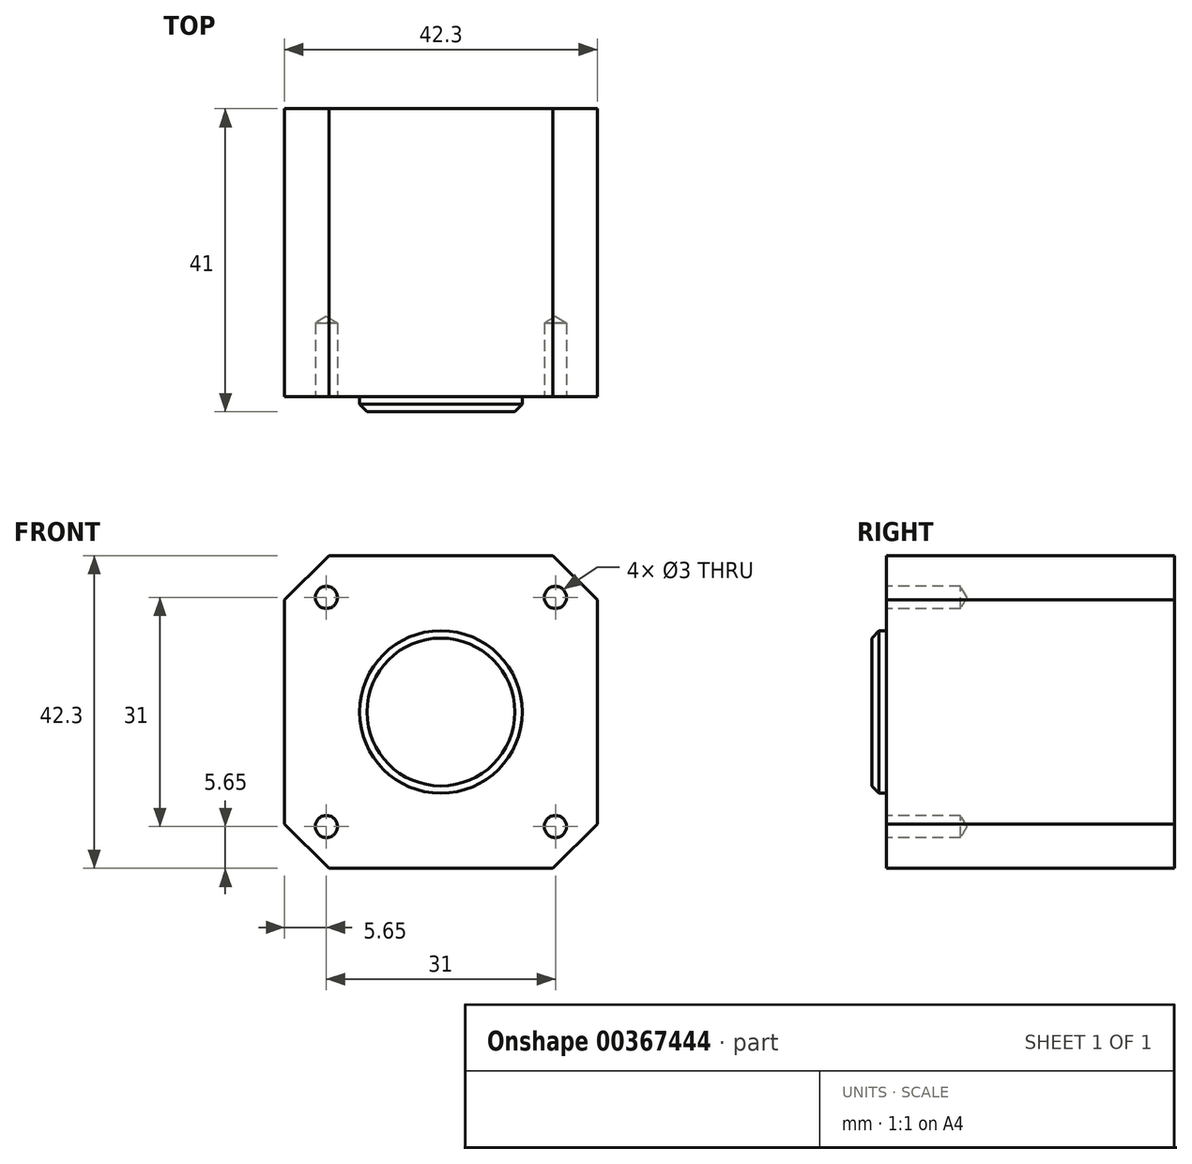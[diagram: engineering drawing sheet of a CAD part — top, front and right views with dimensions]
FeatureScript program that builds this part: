
annotation { "Feature Type Name" : "Feature", "Feature Type Description" : "" }
export const myFeature = defineFeature(function(context is Context, id is Id, definition is map)
    precondition{}
    {
        {
            var Q0;
            Q0=qCreatedBy(makeId("Front.planeOp"),FACE);
            var sketch = newSketch(context, id + "F0", { "sketchPlane" : qUnion([Q0])});
            skLineSegment(sketch, "E0.bottom", {"start": v(0, 0) * mm, "end": v(42.3, 0) * mm});
            skLineSegment(sketch, "E0.top", {"start": v(0, 42.3) * mm, "end": v(42.3, 42.3) * mm});
            skLineSegment(sketch, "E0.left", {"start": v(0, 0) * mm, "end": v(0, 42.3) * mm});
            skLineSegment(sketch, "E0.right", {"start": v(42.3, 0) * mm, "end": v(42.3, 42.3) * mm});
            skSolve(sketch);
        }
        {
            var Q0;
            Q0=makeQuery(id+"F0.imprint","IMPRINT",FACE,{"disambiguationData":[TD([[makeQuery(id+"F0.imprint","IMPRINT",EDGE,{"derivedFrom":sQuery(id+"F0.wireOp",EDGE,"E0.bottom")}),1.0]])]});
            extrude(context, id + "F1", {"entities" : qUnion([Q0]), "depth" : 39 * mm});
        }
        {
            var Q0;
            Q0=makeQuery(id+"F1.opExtrude","CAP_FACE",FACE,{"disambiguationData":[OSD([sQuery(id+"F0.wireOp",EDGE,"E0.bottom"),sQuery(id+"F0.wireOp",EDGE,"E0.top"),sQuery(id+"F0.wireOp",EDGE,"E0.left"),sQuery(id+"F0.wireOp",EDGE,"E0.right")])],"isStart":false});
            var sketch = newSketch(context, id + "F2", { "sketchPlane" : qUnion([Q0])});
            skCircle(sketch, "E1", {"center": v(21.15, 21.15) * mm, "radius": 11 * mm});
            skPoint(sketch, "E1.centerSnap0", {"position": v(42.3, 21.15) * mm});
            skPoint(sketch, "E1.centerSnap1", {"position": v(21.15, 42.3) * mm});
            skSolve(sketch);
        }
        {
            var Q0;
            Q0=qSketchRegion(id+"F2",true);
            extrude(context, id + "F3", {"entities" : qUnion([Q0]), "operationType" : NewBodyOperationType.ADD, "depth" : 2 * mm});
        }
        {
            var Q0;
            Q0=makeQuery(id+"F3.opExtrude","CAP_EDGE",EDGE,{"disambiguationData":[OSD([sQuery(id+"F2.wireOp",EDGE,"E1")])],"isStart":false});
            chamfer(context, id + "F4", {"entities" : qUnion([Q0]), "width" : 1 * mm, "tangentPropagation" : true});
        }
        {
            var Q0;
            Q0=makeQuery(id+"F1.opExtrude","CAP_FACE",FACE,{"disambiguationData":[OSD([sQuery(id+"F0.wireOp",EDGE,"E0.bottom"),sQuery(id+"F0.wireOp",EDGE,"E0.top"),sQuery(id+"F0.wireOp",EDGE,"E0.left"),sQuery(id+"F0.wireOp",EDGE,"E0.right")])],"isStart":false});
            var sketch = newSketch(context, id + "F5", { "sketchPlane" : qUnion([Q0])});
            skLineSegment(sketch, "E2", {"start": v(21.15, 42.3) * mm, "end": v(21.15, 0) * mm, "construction": true});
            skLineSegment(sketch, "E3", {"start": v(42.3, 21.15) * mm, "end": v(0, 21.15) * mm, "construction": true});
            skPoint(sketch, "E4", {"position": v(5.65, 36.65) * mm});
            skPoint(sketch, "E5", {"position": v(36.65, 36.65) * mm});
            skPoint(sketch, "E6", {"position": v(36.65, 5.65) * mm});
            skPoint(sketch, "E7", {"position": v(5.65, 5.65) * mm});
            skSolve(sketch);
        }
        {
            var Q0;
            Q0=sQuery(id+"F5.wireOp",VERTEX,"E4");
            var Q1;
            Q1=sQuery(id+"F5.wireOp",VERTEX,"E5");
            var Q2;
            Q2=sQuery(id+"F5.wireOp",VERTEX,"E6");
            var Q3;
            Q3=sQuery(id+"F5.wireOp",VERTEX,"E7");
            var Q4;
            Q4=makeQuery(id+"F1.opExtrude","SWEPT_BODY",BODY,{"disambiguationData":[OSD([sQuery(id+"F0.wireOp",EDGE,"E0.bottom"),sQuery(id+"F0.wireOp",EDGE,"E0.top"),sQuery(id+"F0.wireOp",EDGE,"E0.left"),sQuery(id+"F0.wireOp",EDGE,"E0.right")])]});
            hole(context, id + "F6", {"style" : HoleStyle.SIMPLE, "endStyle" : HoleEndStyle.BLIND, "holeDiameter" : 3 * mm, "holeDepth" : 10 * mm, "startFromSketch" : true, "locations" : qUnion([Q0, Q1, Q2, Q3]), "scope" : qUnion([Q4])});
        }
        {
            var Q0;
            Q0=makeQuery(id+"F1.opExtrude","SWEPT_EDGE",EDGE,{"disambiguationData":[OSD([sQuery(id+"F0.wireOp",EDGE,"E0.top"),sQuery(id+"F0.wireOp",EDGE,"E0.left")])]});
            var Q1;
            Q1=makeQuery(id+"F1.opExtrude","SWEPT_EDGE",EDGE,{"disambiguationData":[OSD([sQuery(id+"F0.wireOp",EDGE,"E0.bottom"),sQuery(id+"F0.wireOp",EDGE,"E0.left")])]});
            var Q2;
            Q2=makeQuery(id+"F1.opExtrude","SWEPT_EDGE",EDGE,{"disambiguationData":[OSD([sQuery(id+"F0.wireOp",EDGE,"E0.top"),sQuery(id+"F0.wireOp",EDGE,"E0.right")])]});
            var Q3;
            Q3=makeQuery(id+"F1.opExtrude","SWEPT_EDGE",EDGE,{"disambiguationData":[OSD([sQuery(id+"F0.wireOp",EDGE,"E0.bottom"),sQuery(id+"F0.wireOp",EDGE,"E0.right")])]});
            chamfer(context, id + "F7", {"entities" : qUnion([Q0, Q1, Q2, Q3]), "width" : 6 * mm, "tangentPropagation" : true});
        }
    });
